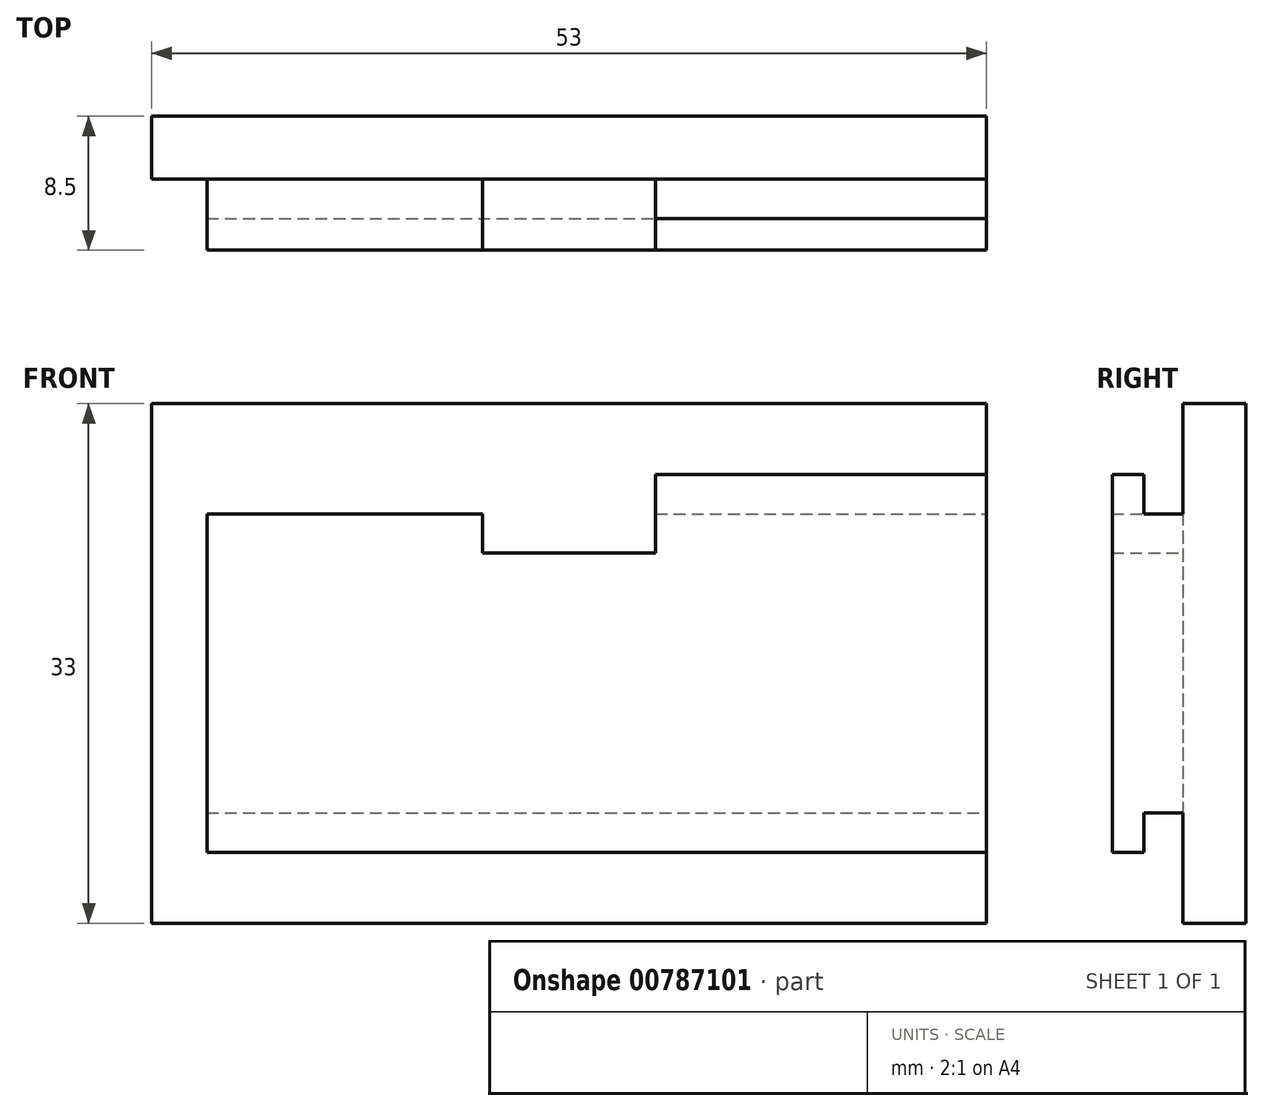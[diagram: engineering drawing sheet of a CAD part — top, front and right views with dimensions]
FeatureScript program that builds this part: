
annotation { "Feature Type Name" : "Feature", "Feature Type Description" : "" }
export const myFeature = defineFeature(function(context is Context, id is Id, definition is map)
    precondition{}
    {
        {
            var Q0;
            Q0=qCreatedBy(makeId("Front.planeOp"),FACE);
            var sketch = newSketch(context, id + "F0", { "sketchPlane" : qUnion([Q0])});
            skLineSegment(sketch, "E0.bottom", {"start": v(-26.5, 16.5) * mm, "end": v(26.5, 16.5) * mm});
            skLineSegment(sketch, "E0.top", {"start": v(-26.5, -16.5) * mm, "end": v(26.5, -16.5) * mm});
            skLineSegment(sketch, "E0.left", {"start": v(-26.5, 16.5) * mm, "end": v(-26.5, -16.5) * mm});
            skLineSegment(sketch, "E0.right", {"start": v(26.5, 16.5) * mm, "end": v(26.5, -16.5) * mm});
            skPoint(sketch, "E0.middle", {"position": v(0, 0) * mm});
            skLineSegment(sketch, "E1.bottom", {"start": v(-23, 12) * mm, "end": v(23, 12) * mm});
            skLineSegment(sketch, "E1.top", {"start": v(-23, -12) * mm, "end": v(23, -12) * mm});
            skLineSegment(sketch, "E1.left", {"start": v(-23, 12) * mm, "end": v(-23, -12) * mm});
            skLineSegment(sketch, "E1.right", {"start": v(23, 12) * mm, "end": v(23, -12) * mm});
            skPoint(sketch, "E2", {"position": v(0, 16.5) * mm});
            skPoint(sketch, "E3", {"position": v(0, 12) * mm});
            skLineSegment(sketch, "E4", {"start": v(0, 16.5) * mm, "end": v(0, 12) * mm});
            skPoint(sketch, "E5", {"position": v(0, 14.25) * mm});
            skLineSegment(sketch, "E6.bottom", {"start": v(-5.5, 16.5) * mm, "end": v(5.5, 16.5) * mm});
            skLineSegment(sketch, "E6.top", {"start": v(-5.5, 12) * mm, "end": v(5.5, 12) * mm});
            skLineSegment(sketch, "E6.left", {"start": v(-5.5, 16.5) * mm, "end": v(-5.5, 12) * mm});
            skLineSegment(sketch, "E6.right", {"start": v(5.5, 16.5) * mm, "end": v(5.5, 12) * mm});
            skLineSegment(sketch, "E7.left", {"start": v(-5.5, 12) * mm, "end": v(-5.5, 12) * mm});
            skLineSegment(sketch, "E7.right", {"start": v(5.5, 12) * mm, "end": v(5.5, 12) * mm});
            skLineSegment(sketch, "E8.top", {"start": v(-5.5, 7) * mm, "end": v(5.5, 7) * mm});
            skLineSegment(sketch, "E8.left", {"start": v(-5.5, 12) * mm, "end": v(-5.5, 7) * mm});
            skLineSegment(sketch, "E8.right", {"start": v(5.5, 12) * mm, "end": v(5.5, 7) * mm});
            skLineSegment(sketch, "E9.top", {"start": v(-23, -9.5) * mm, "end": v(23, -9.5) * mm});
            skLineSegment(sketch, "E9.left", {"start": v(-23, -12) * mm, "end": v(-23, -9.5) * mm});
            skLineSegment(sketch, "E9.right", {"start": v(23, -12) * mm, "end": v(23, -9.5) * mm});
            skLineSegment(sketch, "E10.top", {"start": v(-23, 9.5) * mm, "end": v(23, 9.5) * mm});
            skLineSegment(sketch, "E10.left", {"start": v(-23, 12) * mm, "end": v(-23, 9.5) * mm});
            skLineSegment(sketch, "E10.right", {"start": v(23, 12) * mm, "end": v(23, 9.5) * mm});
            skLineSegment(sketch, "E11.bottom", {"start": v(-23, 9.5) * mm, "end": v(-26.5, 9.5) * mm});
            skLineSegment(sketch, "E11.top", {"start": v(-23, 12) * mm, "end": v(-26.5, 12) * mm});
            skLineSegment(sketch, "E11.left", {"start": v(-23, 9.5) * mm, "end": v(-23, 12) * mm});
            skLineSegment(sketch, "E11.right", {"start": v(-26.5, 9.5) * mm, "end": v(-26.5, 12) * mm});
            skLineSegment(sketch, "E12.bottom", {"start": v(-23, -12) * mm, "end": v(-26.5, -12) * mm});
            skLineSegment(sketch, "E12.top", {"start": v(-23, -9.5) * mm, "end": v(-26.5, -9.5) * mm});
            skLineSegment(sketch, "E12.right", {"start": v(-26.5, -12) * mm, "end": v(-26.5, -9.5) * mm});
            skLineSegment(sketch, "E13.bottom", {"start": v(23, 9.5) * mm, "end": v(26.5, 9.5) * mm});
            skLineSegment(sketch, "E13.top", {"start": v(23, 12) * mm, "end": v(26.5, 12) * mm});
            skLineSegment(sketch, "E13.left", {"start": v(23, 9.5) * mm, "end": v(23, 12) * mm});
            skLineSegment(sketch, "E13.right", {"start": v(26.5, 9.5) * mm, "end": v(26.5, 12) * mm});
            skLineSegment(sketch, "E14.bottom", {"start": v(23, -9.5) * mm, "end": v(26.5, -9.5) * mm});
            skLineSegment(sketch, "E14.top", {"start": v(23, -12) * mm, "end": v(26.5, -12) * mm});
            skLineSegment(sketch, "E14.left", {"start": v(23, -9.5) * mm, "end": v(23, -12) * mm});
            skLineSegment(sketch, "E14.right", {"start": v(26.5, -9.5) * mm, "end": v(26.5, -12) * mm});
            skSolve(sketch);
        }
        {
            var Q0;
            {var subQ1=sQuery(id+"F0.wireOp",EDGE,"E0.top");Q0=makeQuery(id+"F0.imprint","IMPRINT",FACE,{"disambiguationData":[TD([[makeQuery(id+"F0.imprint","IMPRINT",EDGE,{"derivedFrom":subQ1}),1.0]])]});}
            var Q1;
            {var subQ0=sQuery(id+"F0.wireOp",EDGE,"E4");Q1=makeQuery(id+"F0.imprint","IMPRINT",FACE,{"disambiguationData":[TD([[makeQuery(id+"F0.imprint","IMPRINT",EDGE,{"derivedFrom":subQ0}),-1.0]])]});}
            var Q2;
            {var subQ0=sQuery(id+"F0.wireOp",EDGE,"E4");Q2=makeQuery(id+"F0.imprint","IMPRINT",FACE,{"disambiguationData":[TD([[makeQuery(id+"F0.imprint","IMPRINT",EDGE,{"derivedFrom":subQ0}),1.0]])]});}
            var Q3;
            {var subQ0=sQuery(id+"F0.wireOp",EDGE,"E6.left");Q3=makeQuery(id+"F0.imprint","IMPRINT",FACE,{"disambiguationData":[TD([[makeQuery(id+"F0.imprint","IMPRINT",EDGE,{"derivedFrom":subQ0}),-1.0]])]});}
            var Q4;
            {var subQ0=sQuery(id+"F0.wireOp",EDGE,"E11.bottom");Q4=makeQuery(id+"F0.imprint","IMPRINT",FACE,{"disambiguationData":[TD([[makeQuery(id+"F0.imprint","IMPRINT",EDGE,{"derivedFrom":subQ0}),-1.0]])]});}
            var Q5;
            {var subQ0=sQuery(id+"F0.wireOp",EDGE,"E11.bottom");Q5=makeQuery(id+"F0.imprint","IMPRINT",FACE,{"disambiguationData":[TD([[makeQuery(id+"F0.imprint","IMPRINT",EDGE,{"derivedFrom":subQ0}),1.0]])]});}
            var Q6;
            {var subQ0=sQuery(id+"F0.wireOp",EDGE,"E12.bottom");Q6=makeQuery(id+"F0.imprint","IMPRINT",FACE,{"disambiguationData":[TD([[makeQuery(id+"F0.imprint","IMPRINT",EDGE,{"derivedFrom":subQ0}),-1.0]])]});}
            var Q7;
            {var subQ0=sQuery(id+"F0.wireOp",EDGE,"E8.left");var subQ3=sQuery(id+"F0.wireOp",EDGE,"E10.top");var subQ4=makeQuery(id+"F0.imprint","INTERSECT",VERTEX,{"derivedFrom":[subQ0,subQ3]});Q7=makeQuery(id+"F0.imprint","IMPRINT",FACE,{"disambiguationData":[TD([[makeQuery(id+"F0.imprint","IMPRINT",EDGE,{"disambiguationData":[TD([[subQ4,-1.0]])],"derivedFrom":subQ3}),1.0]])]});}
            var Q8;
            {var subQ0=sQuery(id+"F0.wireOp",EDGE,"E8.top");Q8=makeQuery(id+"F0.imprint","IMPRINT",FACE,{"disambiguationData":[TD([[makeQuery(id+"F0.imprint","IMPRINT",EDGE,{"derivedFrom":subQ0}),1.0]])]});}
            var Q9;
            {var subQ0=sQuery(id+"F0.wireOp",EDGE,"E6.right");Q9=makeQuery(id+"F0.imprint","IMPRINT",FACE,{"disambiguationData":[TD([[makeQuery(id+"F0.imprint","IMPRINT",EDGE,{"derivedFrom":subQ0}),1.0]])]});}
            var Q10;
            {var subQ0=sQuery(id+"F0.wireOp",EDGE,"E13.bottom");Q10=makeQuery(id+"F0.imprint","IMPRINT",FACE,{"disambiguationData":[TD([[makeQuery(id+"F0.imprint","IMPRINT",EDGE,{"derivedFrom":subQ0}),1.0]])]});}
            var Q11;
            {var subQ0=sQuery(id+"F0.wireOp",EDGE,"E13.bottom");Q11=makeQuery(id+"F0.imprint","IMPRINT",FACE,{"disambiguationData":[TD([[makeQuery(id+"F0.imprint","IMPRINT",EDGE,{"derivedFrom":subQ0}),-1.0]])]});}
            var Q12;
            {var subQ2=sQuery(id+"F0.wireOp",EDGE,"E14.bottom");Q12=makeQuery(id+"F0.imprint","IMPRINT",FACE,{"disambiguationData":[TD([[makeQuery(id+"F0.imprint","IMPRINT",EDGE,{"derivedFrom":subQ2}),-1.0]])]});}
            extrude(context, id + "F1", {"entities" : qUnion([Q0, Q1, Q2, Q3, Q4, Q5, Q6, Q7, Q8, Q9, Q10, Q11, Q12]), "depth" : 4 * mm, "offsetDistance" : 25 * mm});
        }
        {
            var Q0;
            Q0=makeQuery(id+"F0.imprint","IMPRINT",FACE,{"disambiguationData":[TD([[makeQuery(id+"F0.imprint","IMPRINT",EDGE,{"derivedFrom":sQuery(id+"F0.wireOp",EDGE,"E1.top")}),1.0]])]});
            var Q1;
            {var subQ0=sQuery(id+"F0.wireOp",EDGE,"E8.top");Q1=makeQuery(id+"F0.imprint","IMPRINT",FACE,{"disambiguationData":[TD([[makeQuery(id+"F0.imprint","IMPRINT",EDGE,{"derivedFrom":subQ0}),-1.0]])]});}
            var Q2;
            {var subQ5=sQuery(id+"F0.wireOp",EDGE,"E10.left");Q2=makeQuery(id+"F0.imprint","IMPRINT",FACE,{"disambiguationData":[TD([[makeQuery(id+"F0.imprint","IMPRINT",EDGE,{"derivedFrom":subQ5}),1.0]])]});}
            var Q3;
            {var subQ5=sQuery(id+"F0.wireOp",EDGE,"E10.right");Q3=makeQuery(id+"F0.imprint","IMPRINT",FACE,{"disambiguationData":[TD([[makeQuery(id+"F0.imprint","IMPRINT",EDGE,{"derivedFrom":subQ5}),-1.0]])]});}
            var Q4;
            {var subQ0=sQuery(id+"F0.wireOp",EDGE,"E1.top");Q4=makeQuery(id+"F0.imprint","IMPRINT",FACE,{"disambiguationData":[TD([[makeQuery(id+"F0.imprint","IMPRINT",EDGE,{"derivedFrom":subQ0}),1.0]])]});}
            var Q5;
            {var subQ0=sQuery(id+"F0.wireOp",EDGE,"E8.right");var subQ5=sQuery(id+"F0.wireOp",EDGE,"E10.top");var subQ7=makeQuery(id+"F0.imprint","INTERSECT",VERTEX,{"derivedFrom":[subQ0,subQ5]});Q5=makeQuery(id+"F0.imprint","IMPRINT",FACE,{"disambiguationData":[TD([[makeQuery(id+"F0.imprint","IMPRINT",EDGE,{"disambiguationData":[TD([[subQ7,1.0]])],"derivedFrom":subQ0}),1.0]])]});}
            var Q6;
            {var subQ0=sQuery(id+"F0.wireOp",EDGE,"E13.bottom");Q6=makeQuery(id+"F0.imprint","IMPRINT",FACE,{"disambiguationData":[TD([[makeQuery(id+"F0.imprint","IMPRINT",EDGE,{"derivedFrom":subQ0}),1.0]])]});}
            var Q7;
            {var subQ0=sQuery(id+"F0.wireOp",EDGE,"E13.bottom");Q7=makeQuery(id+"F0.imprint","IMPRINT",FACE,{"disambiguationData":[TD([[makeQuery(id+"F0.imprint","IMPRINT",EDGE,{"derivedFrom":subQ0}),-1.0]])]});}
            var Q8;
            {var subQ2=sQuery(id+"F0.wireOp",EDGE,"E14.bottom");Q8=makeQuery(id+"F0.imprint","IMPRINT",FACE,{"disambiguationData":[TD([[makeQuery(id+"F0.imprint","IMPRINT",EDGE,{"derivedFrom":subQ2}),-1.0]])]});}
            extrude(context, id + "F2", {"entities" : qUnion([Q0, Q1, Q2, Q3, Q4, Q5, Q6, Q7, Q8]), "operationType" : NewBodyOperationType.ADD, "depth" : 8.5 * mm, "offsetDistance" : 25 * mm});
        }
        {
            var Q0;
            {var subQ0=sQuery(id+"F0.wireOp",EDGE,"E4");Q0=makeQuery(id+"F0.imprint","IMPRINT",FACE,{"disambiguationData":[TD([[makeQuery(id+"F0.imprint","IMPRINT",EDGE,{"derivedFrom":subQ0}),-1.0]])]});}
            var Q1;
            {var subQ0=sQuery(id+"F0.wireOp",EDGE,"E4");Q1=makeQuery(id+"F0.imprint","IMPRINT",FACE,{"disambiguationData":[TD([[makeQuery(id+"F0.imprint","IMPRINT",EDGE,{"derivedFrom":subQ0}),1.0]])]});}
            extrude(context, id + "F3", {"entities" : qUnion([Q0, Q1]), "operationType" : NewBodyOperationType.ADD, "depth" : 1 * mm, "offsetDistance" : 25 * mm});
        }
        {
            var Q0;
            {var subQ0=sQuery(id+"F0.wireOp",EDGE,"E8.right");var subQ5=sQuery(id+"F0.wireOp",EDGE,"E10.top");var subQ7=makeQuery(id+"F0.imprint","INTERSECT",VERTEX,{"derivedFrom":[subQ0,subQ5]});Q0=makeQuery(id+"F0.imprint","IMPRINT",FACE,{"disambiguationData":[TD([[makeQuery(id+"F0.imprint","IMPRINT",EDGE,{"disambiguationData":[TD([[subQ7,1.0]])],"derivedFrom":subQ0}),1.0]])]});}
            var Q1;
            {var subQ0=sQuery(id+"F0.wireOp",EDGE,"E1.top");Q1=makeQuery(id+"F0.imprint","IMPRINT",FACE,{"disambiguationData":[TD([[makeQuery(id+"F0.imprint","IMPRINT",EDGE,{"derivedFrom":subQ0}),1.0]])]});}
            var Q2;
            {var subQ0=sQuery(id+"F0.wireOp",EDGE,"E13.bottom");Q2=makeQuery(id+"F0.imprint","IMPRINT",FACE,{"disambiguationData":[TD([[makeQuery(id+"F0.imprint","IMPRINT",EDGE,{"derivedFrom":subQ0}),1.0]])]});}
            var Q3;
            {var subQ2=sQuery(id+"F0.wireOp",EDGE,"E14.bottom");Q3=makeQuery(id+"F0.imprint","IMPRINT",FACE,{"disambiguationData":[TD([[makeQuery(id+"F0.imprint","IMPRINT",EDGE,{"derivedFrom":subQ2}),-1.0]])]});}
            extrude(context, id + "F4", {"entities" : qUnion([Q0, Q1, Q2, Q3]), "operationType" : NewBodyOperationType.REMOVE, "depth" : 6.5 * mm, "offsetDistance" : 25 * mm});
        }
        {
            var Q0;
            {var subQ5=sQuery(id+"F0.wireOp",EDGE,"E10.right");Q0=makeQuery(id+"F0.imprint","IMPRINT",FACE,{"disambiguationData":[TD([[makeQuery(id+"F0.imprint","IMPRINT",EDGE,{"derivedFrom":subQ5}),-1.0]])]});}
            var Q1;
            {var subQ5=sQuery(id+"F0.wireOp",EDGE,"E10.left");Q1=makeQuery(id+"F0.imprint","IMPRINT",FACE,{"disambiguationData":[TD([[makeQuery(id+"F0.imprint","IMPRINT",EDGE,{"derivedFrom":subQ5}),1.0]])]});}
            var Q2;
            {var subQ0=sQuery(id+"F0.wireOp",EDGE,"E1.top");Q2=makeQuery(id+"F0.imprint","IMPRINT",FACE,{"disambiguationData":[TD([[makeQuery(id+"F0.imprint","IMPRINT",EDGE,{"derivedFrom":subQ0}),1.0]])]});}
            var Q3;
            {var subQ0=sQuery(id+"F0.wireOp",EDGE,"E13.bottom");Q3=makeQuery(id+"F0.imprint","IMPRINT",FACE,{"disambiguationData":[TD([[makeQuery(id+"F0.imprint","IMPRINT",EDGE,{"derivedFrom":subQ0}),1.0]])]});}
            var Q4;
            {var subQ0=sQuery(id+"F0.wireOp",EDGE,"E8.right");var subQ5=sQuery(id+"F0.wireOp",EDGE,"E10.top");var subQ7=makeQuery(id+"F0.imprint","INTERSECT",VERTEX,{"derivedFrom":[subQ0,subQ5]});Q4=makeQuery(id+"F0.imprint","IMPRINT",FACE,{"disambiguationData":[TD([[makeQuery(id+"F0.imprint","IMPRINT",EDGE,{"disambiguationData":[TD([[subQ7,1.0]])],"derivedFrom":subQ0}),1.0]])]});}
            var Q5;
            {var subQ2=sQuery(id+"F0.wireOp",EDGE,"E14.bottom");Q5=makeQuery(id+"F0.imprint","IMPRINT",FACE,{"disambiguationData":[TD([[makeQuery(id+"F0.imprint","IMPRINT",EDGE,{"derivedFrom":subQ2}),-1.0]])]});}
            var Q6;
            {var subQ3=sQuery(id+"F0.wireOp",EDGE,"E8.left");var subQ5=sQuery(id+"F0.wireOp",EDGE,"E10.top");var subQ7=makeQuery(id+"F0.imprint","INTERSECT",VERTEX,{"derivedFrom":[subQ3,subQ5]});Q6=makeQuery(id+"F0.imprint","IMPRINT",FACE,{"disambiguationData":[TD([[makeQuery(id+"F0.imprint","IMPRINT",EDGE,{"disambiguationData":[TD([[subQ7,1.0]])],"derivedFrom":subQ3}),-1.0]])]});}
            extrude(context, id + "F5", {"entities" : qUnion([Q0, Q1, Q2, Q3, Q4, Q5, Q6]), "operationType" : NewBodyOperationType.ADD, "depth" : 4 * mm, "offsetDistance" : 25 * mm});
        }
    });
